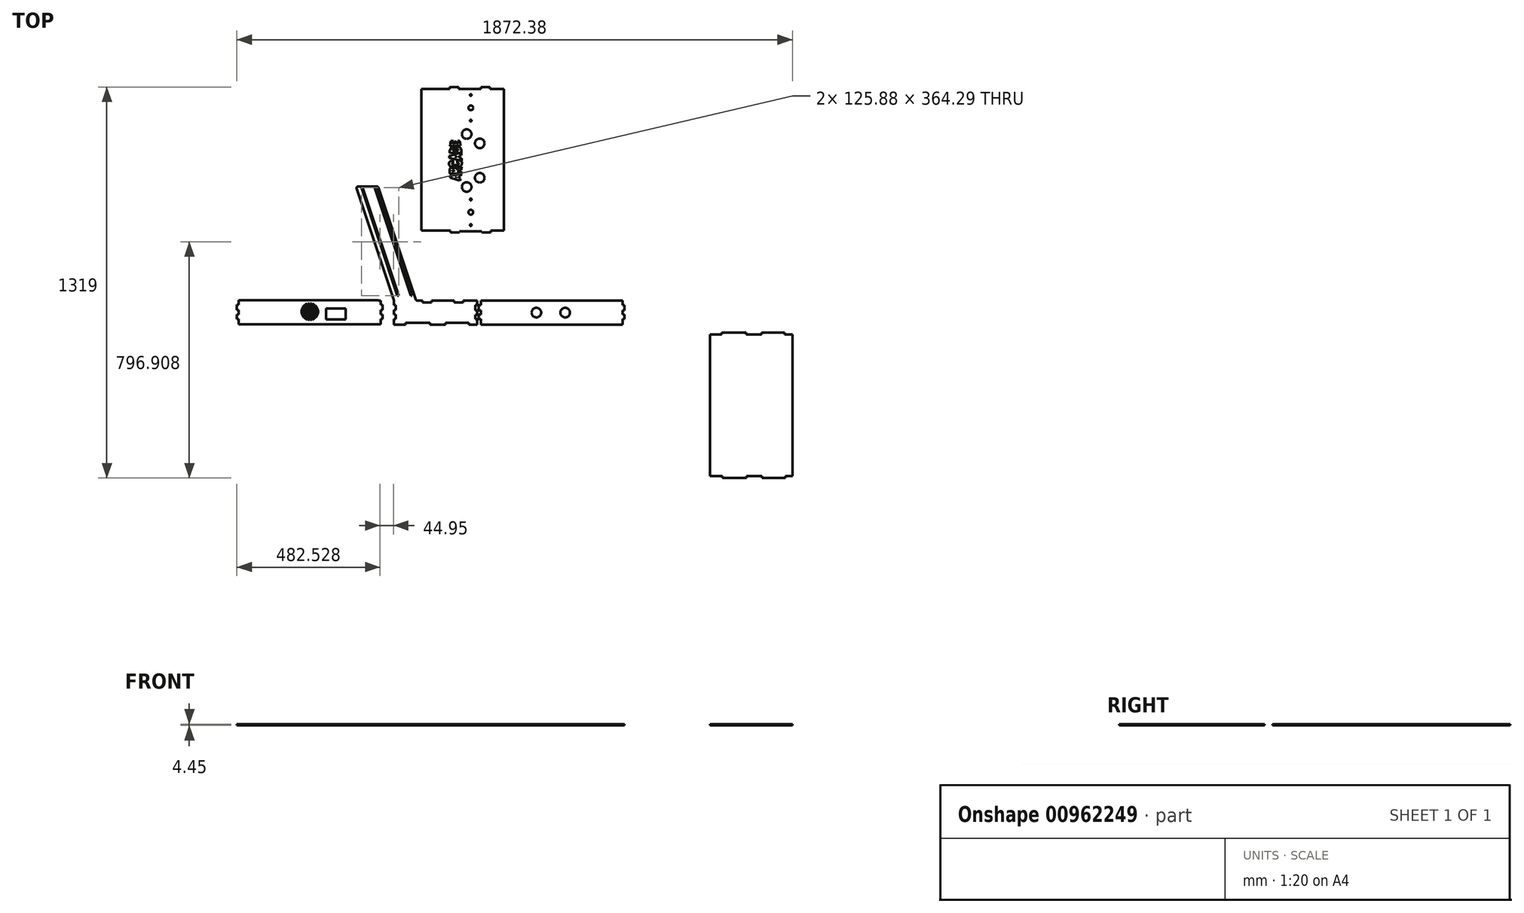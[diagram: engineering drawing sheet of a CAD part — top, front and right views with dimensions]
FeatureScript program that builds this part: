
annotation { "Feature Type Name" : "Feature", "Feature Type Description" : "" }
export const myFeature = defineFeature(function(context is Context, id is Id, definition is map)
    precondition{}
    {
        {
            var Q0;
            Q0=qCreatedBy(makeId("Top.planeOp"),FACE);
            var sketch = newSketch(context, id + "F0", { "sketchPlane" : qUnion([Q0])});
            skLineSegment(sketch, "E0.0", {"start": v(-133.22, 195.57) * mm, "end": v(-13.13, -164.7) * mm});
            skLineSegment(sketch, "E0.2", {"start": v(-206.4, 192.41) * mm, "end": v(-84, -174.81) * mm});
            skLineSegment(sketch, "E1", {"start": v(-84, -174.81) * mm, "end": v(-80.85, -184.23) * mm});
            skLineSegment(sketch, "E2", {"start": v(-13.13, -164.7) * mm, "end": v(-7.25, -182.33) * mm});
            skPoint(sketch, "E3.start.orphan", {"position": v(-23.94, -169.52) * mm});
            skLineSegment(sketch, "E4.bottom", {"start": v(-2.51, -185.75) * mm, "end": v(15.83, -185.75) * mm});
            skLineSegment(sketch, "E5", {"start": v(-129.53, 12.4) * mm, "end": v(-125.08, 12.4) * mm});
            skLineSegment(sketch, "E6", {"start": v(-89.03, 12.4) * mm, "end": v(-93.48, 12.4) * mm});
            skLineSegment(sketch, "E7.left", {"start": v(-80.35, -185.75) * mm, "end": v(-80.35, -201.04) * mm});
            skPoint(sketch, "E8.end.orphan", {"position": v(-48.56, -185.75) * mm});
            skLineSegment(sketch, "E9", {"start": v(-188.02, 199) * mm, "end": v(-201.66, 199) * mm});
            skLineSegment(sketch, "E10", {"start": v(-188.02, 199) * mm, "end": v(-137.97, 199) * mm});
            skPoint(sketch, "E11.start.orphan", {"position": v(-188.02, 194.54) * mm});
            skLineSegment(sketch, "E12.bottom", {"start": v(45.83, -192.08) * mm, "end": v(15.83, -192.08) * mm});
            skPoint(sketch, "E12.middle", {"position": v(31.62, -185.75) * mm});
            skPoint(sketch, "E13.middle", {"position": v(159.6, -185.75) * mm});
            skPoint(sketch, "E12.top.end.orphan", {"position": v(17.41, -179.42) * mm});
            skPoint(sketch, "E14.orphan", {"position": v(47.41, -179.42) * mm});
            skPoint(sketch, "E13.top.end.orphan", {"position": v(142.34, -174.18) * mm});
            skPoint(sketch, "E15.orphan", {"position": v(176.85, -174.18) * mm});
            skLineSegment(sketch, "E16.bottom", {"start": v(152.59, -192.08) * mm, "end": v(122.59, -192.08) * mm});
            skLineSegment(sketch, "E16.left", {"start": v(152.59, -192.08) * mm, "end": v(152.58, -185.75) * mm});
            skLineSegment(sketch, "E16.right", {"start": v(122.59, -192.08) * mm, "end": v(122.58, -185.75) * mm});
            skLineSegment(sketch, "E17.trimOffspring", {"start": v(47.28, -185.75) * mm, "end": v(122.58, -185.75) * mm});
            skLineSegment(sketch, "E18.trimOffspring", {"start": v(152.58, -185.75) * mm, "end": v(199.85, -185.75) * mm});
            skPoint(sketch, "E19.middle", {"position": v(199.48, -209.33) * mm});
            skPoint(sketch, "E19.left.end.orphan", {"position": v(205.95, -200.47) * mm});
            skPoint(sketch, "E20.orphan", {"position": v(205.67, -218.2) * mm});
            skLineSegment(sketch, "E21.bottom", {"start": v(109.66, 43.6) * mm, "end": v(139.96, 43.6) * mm});
            skLineSegment(sketch, "E21.left", {"start": v(109.66, 43.6) * mm, "end": v(109.66, 49.94) * mm});
            skLineSegment(sketch, "E21.right", {"start": v(139.96, 43.6) * mm, "end": v(139.96, 48.06) * mm});
            skLineSegment(sketch, "E22.top", {"start": v(214.96, 43.6) * mm, "end": v(245.26, 43.6) * mm});
            skLineSegment(sketch, "E22.left", {"start": v(214.96, 48.06) * mm, "end": v(214.96, 43.6) * mm});
            skLineSegment(sketch, "E22.right", {"start": v(245.26, 49.94) * mm, "end": v(245.26, 43.6) * mm});
            skLineSegment(sketch, "E23", {"start": v(86.13, 49.94) * mm, "end": v(109.66, 49.94) * mm});
            skLineSegment(sketch, "E24", {"start": v(139.96, 48.06) * mm, "end": v(214.96, 48.06) * mm});
            skLineSegment(sketch, "E25", {"start": v(245.26, 49.94) * mm, "end": v(289.7, 49.94) * mm});
            skLineSegment(sketch, "E26", {"start": v(289.7, 49.94) * mm, "end": v(289.7, 528.39) * mm});
            skLineSegment(sketch, "E27", {"start": v(86.13, 528.39) * mm, "end": v(107.63, 528.39) * mm});
            skLineSegment(sketch, "E28.MirrorCS", {"start": v(107.63, 534.72) * mm, "end": v(107.63, 528.39) * mm});
            skLineSegment(sketch, "E29.MirrorCS", {"start": v(137.93, 534.72) * mm, "end": v(137.93, 528.39) * mm});
            skLineSegment(sketch, "E30.MirrorCS", {"start": v(212.93, 528.39) * mm, "end": v(212.93, 534.72) * mm});
            skLineSegment(sketch, "E31.MirrorCS", {"start": v(243.23, 528.39) * mm, "end": v(243.23, 534.72) * mm});
            skLineSegment(sketch, "E32.trimOffspring", {"start": v(137.93, 528.39) * mm, "end": v(212.93, 528.39) * mm});
            skLineSegment(sketch, "E33.trimOffspring", {"start": v(243.23, 528.39) * mm, "end": v(289.7, 528.39) * mm});
            skPoint(sketch, "E34.start.orphan", {"position": v(86.13, 289.16) * mm});
            skCircle(sketch, "E35", {"center": v(178.38, 507.69) * mm, "radius": 3 * mm});
            skCircle(sketch, "E36", {"center": v(178.38, 421.29) * mm, "radius": 3 * mm});
            skCircle(sketch, "E37", {"center": v(164.4, 375.88) * mm, "radius": 16.13 * mm});
            skCircle(sketch, "E38", {"center": v(208.47, 344.63) * mm, "radius": 16.13 * mm});
            skCircle(sketch, "E39.MirrorC", {"center": v(178.38, 155.57) * mm, "radius": 3 * mm});
            skCircle(sketch, "E40.MirrorC", {"center": v(178.38, 69.17) * mm, "radius": 3 * mm});
            skCircle(sketch, "E41.MirrorC", {"center": v(208.47, 228.58) * mm, "radius": 16.13 * mm});
            skCircle(sketch, "E42.MirrorC", {"center": v(164.4, 197.33) * mm, "radius": 16.13 * mm});
            skCircle(sketch, "E43", {"center": v(178.38, 464.49) * mm, "radius": 8.09 * mm});
            skCircle(sketch, "E44.MirrorC", {"center": v(178.38, 112.37) * mm, "radius": 8.09 * mm});
            skLineSegment(sketch, "E45.MirrorCS", {"start": v(120.12, 254.5) * mm, "end": v(118.38, 254.37) * mm});
            skLineSegment(sketch, "E46.MirrorCS", {"start": v(146.92, 313.16) * mm, "end": v(146.92, 304.04) * mm});
            skLineSegment(sketch, "E47.MirrorCS", {"start": v(146.24, 313.22) * mm, "end": v(146.92, 313.16) * mm});
            skLineSegment(sketch, "E48.MirrorCS", {"start": v(117.25, 254.08) * mm, "end": v(116.34, 253.4) * mm});
            skLineSegment(sketch, "E49.MirrorCS", {"start": v(116.34, 253.4) * mm, "end": v(116, 250.63) * mm});
            skLineSegment(sketch, "E50.MirrorCS", {"start": v(129.87, 228.95) * mm, "end": v(129.87, 231.1) * mm});
            skLineSegment(sketch, "E51.MirrorCS", {"start": v(118.38, 254.37) * mm, "end": v(117.25, 254.08) * mm});
            skLineSegment(sketch, "E52.MirrorCS", {"start": v(121.7, 253.4) * mm, "end": v(120.12, 254.5) * mm});
            skLineSegment(sketch, "E53.MirrorCS", {"start": v(142.11, 234.25) * mm, "end": v(144.38, 234.25) * mm});
            skLineSegment(sketch, "E54.MirrorCS", {"start": v(123.2, 262.9) * mm, "end": v(122.67, 262.98) * mm});
            skLineSegment(sketch, "E55.MirrorCS", {"start": v(116, 250.63) * mm, "end": v(121.7, 250.43) * mm});
            skLineSegment(sketch, "E56.MirrorCS", {"start": v(144.64, 304.04) * mm, "end": v(140.36, 303.04) * mm});
            skLineSegment(sketch, "E57.MirrorCS", {"start": v(121.7, 250.43) * mm, "end": v(121.7, 253.4) * mm});
            skLineSegment(sketch, "E58.MirrorCS", {"start": v(130.78, 258.7) * mm, "end": v(128.56, 260.6) * mm});
            skLineSegment(sketch, "E59.MirrorCS", {"start": v(145.83, 241.97) * mm, "end": v(144.38, 234.25) * mm});
            skLineSegment(sketch, "E60.MirrorCS", {"start": v(138.33, 233.06) * mm, "end": v(142.11, 234.25) * mm});
            skLineSegment(sketch, "E61.MirrorCS", {"start": v(145.08, 255.03) * mm, "end": v(146.64, 255.34) * mm});
            skLineSegment(sketch, "E62.MirrorCS", {"start": v(142.65, 241.97) * mm, "end": v(145.83, 241.97) * mm});
            skLineSegment(sketch, "E63.MirrorCS", {"start": v(140.36, 296.24) * mm, "end": v(145.28, 294.98) * mm});
            skLineSegment(sketch, "E64.MirrorCS", {"start": v(146.92, 304.04) * mm, "end": v(144.64, 304.04) * mm});
            skLineSegment(sketch, "E65.MirrorCS", {"start": v(145.9, 250.5) * mm, "end": v(132.72, 250.5) * mm});
            skLineSegment(sketch, "E66.MirrorCS", {"start": v(140.36, 303.04) * mm, "end": v(140.36, 296.24) * mm});
            skLineSegment(sketch, "E67.MirrorCS", {"start": v(125.05, 299.5) * mm, "end": v(130.81, 298.2) * mm});
            skLineSegment(sketch, "E68.MirrorCS", {"start": v(129.87, 231.1) * mm, "end": v(125.64, 230.28) * mm});
            skLineSegment(sketch, "E69.MirrorCS", {"start": v(123, 224.26) * mm, "end": v(134.99, 220.38) * mm});
            skLineSegment(sketch, "E70.MirrorCS", {"start": v(145.28, 294.98) * mm, "end": v(147.53, 294.98) * mm});
            skLineSegment(sketch, "E71.MirrorCS", {"start": v(130.81, 298.2) * mm, "end": v(130.81, 300.81) * mm});
            skLineSegment(sketch, "E72.MirrorCS", {"start": v(145.62, 242.56) * mm, "end": v(145.9, 250.5) * mm});
            skLineSegment(sketch, "E73.MirrorCS", {"start": v(125.64, 230.28) * mm, "end": v(129.87, 228.95) * mm});
            skLineSegment(sketch, "E74.MirrorCS", {"start": v(141.03, 226.32) * mm, "end": v(137.8, 226.9) * mm});
            skLineSegment(sketch, "E75.MirrorCS", {"start": v(137.8, 226.9) * mm, "end": v(138.33, 233.06) * mm});
            skLineSegment(sketch, "E76.MirrorCS", {"start": v(132.72, 250.5) * mm, "end": v(145.08, 255.03) * mm});
            skLineSegment(sketch, "E77.MirrorCS", {"start": v(147.3, 264.53) * mm, "end": v(130.78, 258.7) * mm});
            skLineSegment(sketch, "E78.MirrorCS", {"start": v(146.64, 255.34) * mm, "end": v(147.3, 264.53) * mm});
            skLineSegment(sketch, "E79.MirrorCS", {"start": v(130.81, 300.81) * mm, "end": v(125.05, 299.5) * mm});
            skLineSegment(sketch, "E80.MirrorCS", {"start": v(143.46, 226.32) * mm, "end": v(141.03, 226.32) * mm});
            skLineSegment(sketch, "E81.MirrorCS", {"start": v(142.65, 241.97) * mm, "end": v(128.56, 238.4) * mm});
            skLineSegment(sketch, "E82.MirrorCS", {"start": v(140.12, 218.92) * mm, "end": v(141.84, 218.2) * mm});
            skLineSegment(sketch, "E83.MirrorCS", {"start": v(135.95, 321.28) * mm, "end": v(135.67, 323.92) * mm});
            skArc(sketch, "E84.MirrorCS", {"start": v(135.67, 323.92) * mm, "mid": v(126.36, 327.54) * mm, "end": v(117.25, 323.41) * mm});
            skLineSegment(sketch, "E85.MirrorCS", {"start": v(107.46, 243.91) * mm, "end": v(145.62, 242.56) * mm});
            skLineSegment(sketch, "E86.MirrorCS", {"start": v(141.84, 218.2) * mm, "end": v(143.46, 226.32) * mm});
            skFitSpline(sketch, "E87.MirrorCS", {"points": [v(128.56, 260.6) * mm, v(123.2, 262.9) * mm, v(114.65, 262.9) * mm, v(107.11, 257.92) * mm, v(107.34, 246.66) * mm, v(107.46, 243.91) * mm, v(131.36, 256.58) * mm, v(128.56, 260.6) * mm]});
            skLineSegment(sketch, "E88.MirrorCS", {"start": v(117.25, 321.28) * mm, "end": v(135.95, 321.28) * mm});
            skLineSegment(sketch, "E89.MirrorCS", {"start": v(131.27, 342.19) * mm, "end": v(130.03, 350.78) * mm});
            skArc(sketch, "E90.MirrorCS", {"start": v(146.24, 324.8) * mm, "mid": v(125.43, 335.33) * mm, "end": v(107.15, 320.84) * mm});
            skLineSegment(sketch, "E91.MirrorCS", {"start": v(108.97, 235.06) * mm, "end": v(109.67, 228.58) * mm});
            skLineSegment(sketch, "E92.MirrorCS", {"start": v(117.25, 341.92) * mm, "end": v(119.47, 353.18) * mm});
            skLineSegment(sketch, "E93.MirrorCS", {"start": v(122.84, 350.78) * mm, "end": v(122.84, 341.92) * mm});
            skLineSegment(sketch, "E94.MirrorCS", {"start": v(134.15, 353.36) * mm, "end": v(135.67, 342.82) * mm});
            skLineSegment(sketch, "E95.MirrorCS", {"start": v(109.67, 228.58) * mm, "end": v(123, 224.26) * mm});
            skLineSegment(sketch, "E96.MirrorCS", {"start": v(119.47, 353.18) * mm, "end": v(111.45, 352.62) * mm});
            skLineSegment(sketch, "E97.MirrorCS", {"start": v(135.67, 342.82) * mm, "end": v(131.27, 342.19) * mm});
            skLineSegment(sketch, "E98.MirrorCS", {"start": v(117.25, 323.41) * mm, "end": v(117.25, 321.28) * mm});
            skLineSegment(sketch, "E99.MirrorCS", {"start": v(147.5, 285.67) * mm, "end": v(105.6, 295.49) * mm});
            skLineSegment(sketch, "E100.MirrorCS", {"start": v(141.7, 353.36) * mm, "end": v(134.15, 353.36) * mm});
            skLineSegment(sketch, "E101.MirrorCS", {"start": v(105.6, 295.49) * mm, "end": v(105.6, 302.4) * mm});
            skLineSegment(sketch, "E102.MirrorCS", {"start": v(130.03, 350.78) * mm, "end": v(122.84, 350.78) * mm});
            skLineSegment(sketch, "E103.MirrorCS", {"start": v(128.56, 238.4) * mm, "end": v(108.97, 235.06) * mm});
            skLineSegment(sketch, "E104.MirrorCS", {"start": v(122.84, 341.92) * mm, "end": v(117.25, 341.92) * mm});
            skLineSegment(sketch, "E105.MirrorCS", {"start": v(111.45, 352.62) * mm, "end": v(108.28, 334.85) * mm});
            skLineSegment(sketch, "E106.MirrorCS", {"start": v(134.99, 220.38) * mm, "end": v(140.12, 218.92) * mm});
            skLineSegment(sketch, "E107.MirrorCS", {"start": v(146.92, 313.7) * mm, "end": v(146.24, 324.8) * mm});
            skLineSegment(sketch, "E108.MirrorCS", {"start": v(105.6, 302.4) * mm, "end": v(146.24, 313.22) * mm});
            skLineSegment(sketch, "E109.MirrorCS", {"start": v(106.5, 312.6) * mm, "end": v(146.92, 313.7) * mm});
            skLineSegment(sketch, "E110.MirrorCS", {"start": v(106.5, 312.6) * mm, "end": v(107.15, 320.84) * mm});
            skLineSegment(sketch, "E111.MirrorCS", {"start": v(143.98, 337.2) * mm, "end": v(141.7, 353.36) * mm});
            skLineSegment(sketch, "E112.MirrorCS", {"start": v(108.28, 334.85) * mm, "end": v(143.98, 337.2) * mm});
            skFitSpline(sketch, "E113.MirrorC", {"points": [v(118.4, 278.2) * mm, v(116.6, 278.05) * mm, v(114.9, 277.2) * mm, v(114.56, 275.62) * mm, v(115.92, 274) * mm, v(121.92, 272.13) * mm, v(128.49, 271.77) * mm, v(134.71, 272.58) * mm, v(138, 274.5) * mm, v(138.34, 276.84) * mm, v(135.73, 277.9) * mm, v(132.68, 278.86) * mm, v(132.68, 279.68) * mm, v(132.62, 286.61) * mm, v(132.68, 287.83) * mm, v(142.87, 285.6) * mm, v(143.54, 285.19) * mm, v(147.96, 281.4) * mm, v(148.3, 273.3) * mm, v(145.36, 268.33) * mm, v(137.77, 264.48) * mm, v(126.67, 263.32) * mm, v(115.01, 264.89) * mm, v(108.45, 268.48) * mm, v(105.05, 272.38) * mm, v(104.54, 276.89) * mm, v(106.18, 281.85) * mm, v(112.01, 286) * mm, v(117.28, 287.53) * mm, v(118.4, 287.58) * mm, v(118.64, 285.19) * mm, v(118.4, 278.2) * mm]});
            skLineSegment(sketch, "E114", {"start": v(147.53, 294.98) * mm, "end": v(147.5, 285.67) * mm});
            skLineSegment(sketch, "E115.bottom", {"start": v(211.85, -185.75) * mm, "end": v(690.3, -185.75) * mm});
            skLineSegment(sketch, "E115.top", {"start": v(211.85, -266.77) * mm, "end": v(690.3, -266.77) * mm});
            skLineSegment(sketch, "E115.left", {"start": v(211.85, -185.75) * mm, "end": v(211.85, -200.65) * mm});
            skLineSegment(sketch, "E115.right", {"start": v(690.3, -185.75) * mm, "end": v(690.3, -200.9) * mm});
            skLineSegment(sketch, "E116.top", {"start": v(211.85, -218.2) * mm, "end": v(205.52, -218.2) * mm});
            skLineSegment(sketch, "E117.top", {"start": v(211.85, -248.5) * mm, "end": v(205.52, -248.5) * mm});
            skLineSegment(sketch, "E117.right", {"start": v(205.52, -233.2) * mm, "end": v(205.52, -248.5) * mm});
            skCircle(sketch, "E118", {"center": v(399.44, -226.26) * mm, "radius": 16.13 * mm});
            skPoint(sketch, "E118.centerSnap0", {"position": v(211.85, -226.26) * mm});
            skCircle(sketch, "E119.MirrorC", {"center": v(496.38, -226.26) * mm, "radius": 16.13 * mm});
            skPoint(sketch, "E120.start.orphan", {"position": v(451.07, -185.75) * mm});
            skLineSegment(sketch, "E121.MirrorCS", {"start": v(690.3, -233.2) * mm, "end": v(696.63, -233.2) * mm});
            skLineSegment(sketch, "E122.MirrorCS", {"start": v(690.3, -248.5) * mm, "end": v(696.63, -248.5) * mm});
            skLineSegment(sketch, "E123.MirrorCS", {"start": v(690.3, -218.2) * mm, "end": v(696.63, -218.2) * mm});
            skLineSegment(sketch, "E124.MirrorCS", {"start": v(690.3, -200.9) * mm, "end": v(696.63, -200.9) * mm});
            skLineSegment(sketch, "E125.trimOffspring", {"start": v(211.85, -218.2) * mm, "end": v(211.85, -226.26) * mm});
            skLineSegment(sketch, "E126.trimOffspring", {"start": v(211.85, -248.5) * mm, "end": v(211.85, -266.77) * mm});
            skLineSegment(sketch, "E127.trimOffspring", {"start": v(690.3, -248.5) * mm, "end": v(690.3, -266.77) * mm});
            skLineSegment(sketch, "E128.trimOffspring", {"start": v(690.3, -218.2) * mm, "end": v(690.3, -233.2) * mm});
            skPoint(sketch, "E129.start.orphan", {"position": v(58.75, -264.57) * mm});
            skPoint(sketch, "E130.middle", {"position": v(-577.81, -208.7) * mm});
            skPoint(sketch, "E130.left.end.orphan", {"position": v(-573.36, -199.94) * mm});
            skPoint(sketch, "E131.orphan", {"position": v(-573.36, -217.46) * mm});
            skLineSegment(sketch, "E132.bottom", {"start": v(-603.58, -184.65) * mm, "end": v(-133.22, -184.65) * mm});
            skLineSegment(sketch, "E132.top", {"start": v(-603.58, -265.67) * mm, "end": v(-125.08, -265.67) * mm});
            skLineSegment(sketch, "E132.left", {"start": v(-603.58, -184.65) * mm, "end": v(-603.58, -199.79) * mm});
            skLineSegment(sketch, "E132.right", {"start": v(-125.08, -185.75) * mm, "end": v(-125.08, -199.79) * mm});
            skLineSegment(sketch, "E133.bottom", {"start": v(-603.58, -199.79) * mm, "end": v(-609.9, -199.79) * mm});
            skLineSegment(sketch, "E133.top", {"start": v(-603.58, -217.09) * mm, "end": v(-609.9, -217.09) * mm});
            skLineSegment(sketch, "E133.right", {"start": v(-609.9, -199.79) * mm, "end": v(-609.9, -217.09) * mm});
            skLineSegment(sketch, "E134.bottom", {"start": v(-603.58, -232.09) * mm, "end": v(-609.9, -232.09) * mm});
            skLineSegment(sketch, "E134.top", {"start": v(-603.58, -247.39) * mm, "end": v(-609.9, -247.39) * mm});
            skLineSegment(sketch, "E134.right", {"start": v(-609.9, -232.09) * mm, "end": v(-609.9, -247.39) * mm});
            skPoint(sketch, "E135.centerSnap0", {"position": v(-563.42, -225.16) * mm});
            skPoint(sketch, "E136.start.orphan", {"position": v(-324.17, -184.65) * mm});
            skLineSegment(sketch, "E137.MirrorCS", {"start": v(-125.08, -247.39) * mm, "end": v(-118.75, -247.39) * mm});
            skLineSegment(sketch, "E138.MirrorCS", {"start": v(-125.08, -217.09) * mm, "end": v(-118.75, -217.09) * mm});
            skLineSegment(sketch, "E139.MirrorCS", {"start": v(-125.08, -199.79) * mm, "end": v(-118.75, -199.79) * mm});
            skLineSegment(sketch, "E140.trimOffspring", {"start": v(-603.58, -217.09) * mm, "end": v(-603.58, -232.09) * mm});
            skLineSegment(sketch, "E141.trimOffspring", {"start": v(-603.58, -247.39) * mm, "end": v(-603.58, -265.67) * mm});
            skLineSegment(sketch, "E142.trimOffspring", {"start": v(-125.08, -247.39) * mm, "end": v(-125.08, -265.67) * mm});
            skLineSegment(sketch, "E143.trimOffspring", {"start": v(-125.08, -217.09) * mm, "end": v(-125.08, -229.04) * mm});
            skPoint(sketch, "E144.middle", {"position": v(0, -266.77) * mm});
            skPoint(sketch, "E145.orphan", {"position": v(1023.86, -273.1) * mm});
            skPoint(sketch, "E146.orphan", {"position": v(1106.14, -273.1) * mm});
            skLineSegment(sketch, "E147.bottom", {"start": v(984.65, -299.5) * mm, "end": v(1023.86, -299.5) * mm});
            skLineSegment(sketch, "E147.left", {"start": v(984.65, -299.5) * mm, "end": v(984.65, -773.5) * mm});
            skLineSegment(sketch, "E148.top", {"start": v(1158.16, -293.17) * mm, "end": v(1236.46, -293.17) * mm});
            skLineSegment(sketch, "E148.left", {"start": v(1158.16, -299.5) * mm, "end": v(1158.16, -293.17) * mm});
            skLineSegment(sketch, "E149.trimOffspring", {"start": v(1106.16, -299.5) * mm, "end": v(1158.16, -299.5) * mm});
            skLineSegment(sketch, "E150.trimOffspring", {"start": v(1240.66, -299.5) * mm, "end": v(1262.47, -299.5) * mm});
            skLineSegment(sketch, "E151.MirrorCS", {"start": v(1026.07, -773.5) * mm, "end": v(1026.07, -777.95) * mm});
            skLineSegment(sketch, "E152.MirrorCS", {"start": v(1108.37, -777.95) * mm, "end": v(1108.37, -784.28) * mm});
            skLineSegment(sketch, "E153.MirrorCS", {"start": v(1160.37, -777.95) * mm, "end": v(1160.37, -784.28) * mm});
            skLineSegment(sketch, "E154.MirrorCS", {"start": v(1238.67, -777.95) * mm, "end": v(1238.67, -784.28) * mm});
            skLineSegment(sketch, "E155.trimOffspring", {"start": v(1108.37, -777.95) * mm, "end": v(1160.37, -777.95) * mm});
            skPoint(sketch, "E156.start.orphan", {"position": v(984.65, -536.5) * mm});
            skLineSegment(sketch, "E157.trimOffspring", {"start": v(1238.67, -777.95) * mm, "end": v(1262.47, -777.95) * mm});
            skLineSegment(sketch, "E158", {"start": v(696.63, -200.9) * mm, "end": v(696.63, -218.2) * mm});
            skLineSegment(sketch, "E159", {"start": v(696.63, -233.2) * mm, "end": v(696.63, -248.5) * mm});
            skLineSegment(sketch, "E160", {"start": v(-118.75, -217.09) * mm, "end": v(-118.75, -199.79) * mm});
            skLineSegment(sketch, "E161", {"start": v(-118.75, -232.09) * mm, "end": v(-118.75, -247.39) * mm});
            skLineSegment(sketch, "E162", {"start": v(107.63, 534.72) * mm, "end": v(137.93, 534.72) * mm});
            skLineSegment(sketch, "E163", {"start": v(212.93, 534.72) * mm, "end": v(243.23, 534.72) * mm});
            skLineSegment(sketch, "E164", {"start": v(1238.67, -784.28) * mm, "end": v(1160.37, -784.28) * mm});
            skLineSegment(sketch, "E165", {"start": v(1108.37, -784.28) * mm, "end": v(1026.07, -784.28) * mm});
            skLineSegment(sketch, "E166", {"start": v(1026.07, -784.28) * mm, "end": v(1026.07, -777.95) * mm});
            skLineSegment(sketch, "E167", {"start": v(984.65, -773.5) * mm, "end": v(984.65, -777.95) * mm});
            skLineSegment(sketch, "E168", {"start": v(984.65, -777.95) * mm, "end": v(1026.07, -777.95) * mm});
            skLineSegment(sketch, "E169.bottom", {"start": v(86.13, 49.94) * mm, "end": v(11.9, 49.94) * mm});
            skLineSegment(sketch, "E169.top", {"start": v(86.13, 528.39) * mm, "end": v(11.9, 528.39) * mm});
            skLineSegment(sketch, "E169.right", {"start": v(11.9, 49.94) * mm, "end": v(11.9, 528.39) * mm});
            skLineSegment(sketch, "E170", {"start": v(-190.32, 194.78) * mm, "end": v(-68.9, -169.52) * mm});
            skLineSegment(sketch, "E171", {"start": v(-64.44, -169.52) * mm, "end": v(-68.9, -169.52) * mm});
            skLineSegment(sketch, "E172", {"start": v(-125.16, 12.63) * mm, "end": v(-185.87, 194.78) * mm});
            skLineSegment(sketch, "E173", {"start": v(-125.16, 12.63) * mm, "end": v(-64.44, -169.52) * mm});
            skLineSegment(sketch, "E174.trimOffspring", {"start": v(-185.87, 194.78) * mm, "end": v(-190.32, 194.78) * mm});
            skLineSegment(sketch, "E175", {"start": v(-140.92, 194.78) * mm, "end": v(-19.5, -169.52) * mm});
            skLineSegment(sketch, "E176", {"start": v(-140.92, 194.78) * mm, "end": v(-145.37, 194.78) * mm});
            skLineSegment(sketch, "E177", {"start": v(-23.94, -169.52) * mm, "end": v(-19.5, -169.52) * mm});
            skLineSegment(sketch, "E178", {"start": v(-84.66, 12.63) * mm, "end": v(-23.94, -169.52) * mm});
            skLineSegment(sketch, "E179", {"start": v(-84.66, 12.63) * mm, "end": v(-145.37, 194.78) * mm});
            skLineSegment(sketch, "E180.top", {"start": v(1023.86, -293.17) * mm, "end": v(1106.16, -293.17) * mm});
            skLineSegment(sketch, "E180.left", {"start": v(1023.86, -299.5) * mm, "end": v(1023.86, -293.17) * mm});
            skLineSegment(sketch, "E180.right", {"start": v(1106.16, -299.5) * mm, "end": v(1106.16, -293.17) * mm});
            skLineSegment(sketch, "E181.MirrorCS", {"start": v(1236.46, -293.17) * mm, "end": v(1158.16, -293.17) * mm});
            skPoint(sketch, "E182.start.orphan", {"position": v(1132.16, -299.5) * mm});
            skPoint(sketch, "E183.orphan", {"position": v(211.85, -232.77) * mm});
            skLineSegment(sketch, "E184", {"start": v(211.85, -218.2) * mm, "end": v(211.85, -230.2) * mm});
            skArc(sketch, "E185", {"start": v(-357.93, -195.94) * mm, "mid": v(-360.4, -195.47) * mm, "end": v(-362.9, -195.23) * mm});
            skPoint(sketch, "E185.centerSnap0", {"position": v(-125.08, -223.06) * mm});
            skPoint(sketch, "E185.centerSnap1", {"position": v(-364.33, -184.65) * mm});
            skLineSegment(sketch, "E186.left", {"start": v(-362.9, -250.9) * mm, "end": v(-362.9, -195.23) * mm});
            skLineSegment(sketch, "E186.right", {"start": v(-365.76, -250.9) * mm, "end": v(-365.76, -195.23) * mm});
            skLineSegment(sketch, "E187.left", {"start": v(-355.09, -249.36) * mm, "end": v(-355.09, -196.77) * mm});
            skLineSegment(sketch, "E187.right", {"start": v(-357.93, -250.19) * mm, "end": v(-357.93, -195.94) * mm});
            skPoint(sketch, "E187.middle", {"position": v(-356.5, -223.06) * mm});
            skPoint(sketch, "E187.middle.positionSnap0", {"position": v(-362.9, -223.06) * mm});
            skPoint(sketch, "E187.centerSnap0", {"position": v(-362.9, -223.06) * mm});
            skLineSegment(sketch, "E188.left", {"start": v(-348.17, -245.77) * mm, "end": v(-348.17, -200.36) * mm});
            skLineSegment(sketch, "E188.right", {"start": v(-345.33, -243.45) * mm, "end": v(-345.33, -202.68) * mm});
            skPoint(sketch, "E188.middle", {"position": v(-346.75, -223.06) * mm});
            skLineSegment(sketch, "E189.MirrorCS", {"start": v(-370.73, -250.19) * mm, "end": v(-370.73, -195.94) * mm});
            skLineSegment(sketch, "E190.MirrorCS", {"start": v(-373.57, -249.36) * mm, "end": v(-373.57, -196.77) * mm});
            skLineSegment(sketch, "E191.MirrorCS", {"start": v(-380.5, -245.77) * mm, "end": v(-380.5, -200.36) * mm});
            skLineSegment(sketch, "E192.MirrorCS", {"start": v(-383.33, -243.45) * mm, "end": v(-383.33, -202.68) * mm});
            skPoint(sketch, "E186.top.end.orphan", {"position": v(-365.76, -191.24) * mm});
            skPoint(sketch, "E186.top.start.orphan", {"position": v(-362.9, -191.24) * mm});
            skPoint(sketch, "E193.orphan", {"position": v(-370.73, -190.18) * mm});
            skPoint(sketch, "E194.orphan", {"position": v(-373.57, -190.18) * mm});
            skPoint(sketch, "E195.orphan", {"position": v(-383.33, -193.02) * mm});
            skPoint(sketch, "E196.orphan", {"position": v(-380.5, -193.02) * mm});
            skPoint(sketch, "E187.top.end.orphan", {"position": v(-357.93, -190.18) * mm});
            skPoint(sketch, "E187.top.start.orphan", {"position": v(-355.09, -190.18) * mm});
            skPoint(sketch, "E188.top.end.orphan", {"position": v(-345.33, -193.02) * mm});
            skPoint(sketch, "E188.top.start.orphan", {"position": v(-348.17, -193.02) * mm});
            skArc(sketch, "E197.trimOffspring", {"start": v(-365.76, -195.23) * mm, "mid": v(-368.26, -195.47) * mm, "end": v(-370.73, -195.94) * mm});
            skArc(sketch, "E198.trimOffspring", {"start": v(-383.33, -202.68) * mm, "mid": v(-392.2, -223.06) * mm, "end": v(-383.33, -243.45) * mm});
            skArc(sketch, "E199.trimOffspring", {"start": v(-370.73, -250.19) * mm, "mid": v(-368.26, -250.65) * mm, "end": v(-365.76, -250.9) * mm});
            skArc(sketch, "E200.trimOffspring", {"start": v(-362.9, -250.9) * mm, "mid": v(-360.4, -250.65) * mm, "end": v(-357.93, -250.19) * mm});
            skArc(sketch, "E201.trimOffspring", {"start": v(-355.09, -249.36) * mm, "mid": v(-351.5, -247.8) * mm, "end": v(-348.17, -245.77) * mm});
            skArc(sketch, "E202.trimOffspring", {"start": v(-345.33, -243.45) * mm, "mid": v(-337.05, -217.36) * mm, "end": v(-355.09, -196.77) * mm});
            skPoint(sketch, "E203.orphan", {"position": v(-370.73, -255.95) * mm});
            skPoint(sketch, "E204.orphan", {"position": v(-373.57, -255.95) * mm});
            skPoint(sketch, "E205.orphan", {"position": v(-380.5, -253.1) * mm});
            skPoint(sketch, "E206.orphan", {"position": v(-383.33, -253.1) * mm});
            skPoint(sketch, "E207.orphan", {"position": v(-362.9, -254.88) * mm});
            skPoint(sketch, "E208.orphan", {"position": v(-357.93, -255.95) * mm});
            skPoint(sketch, "E209.orphan", {"position": v(-355.09, -255.95) * mm});
            skPoint(sketch, "E188.bottom.start.orphan", {"position": v(-348.17, -253.1) * mm});
            skPoint(sketch, "E210.orphan", {"position": v(-345.33, -253.1) * mm});
            skPoint(sketch, "E211.orphan", {"position": v(-365.76, -254.88) * mm});
            skArc(sketch, "E212.trimOffspring", {"start": v(-380.5, -245.77) * mm, "mid": v(-377.16, -247.8) * mm, "end": v(-373.57, -249.36) * mm});
            skArc(sketch, "E213", {"start": v(-373.57, -196.77) * mm, "mid": v(-377.47, -197.73) * mm, "end": v(-380.5, -200.36) * mm});
            skLineSegment(sketch, "E214.bottom", {"start": v(-242.86, -248.61) * mm, "end": v(-309.57, -248.61) * mm});
            skLineSegment(sketch, "E214.top", {"start": v(-242.86, -212.3) * mm, "end": v(-309.57, -212.3) * mm});
            skLineSegment(sketch, "E214.left", {"start": v(-242.86, -248.61) * mm, "end": v(-242.86, -212.3) * mm});
            skLineSegment(sketch, "E214.right", {"start": v(-309.57, -248.61) * mm, "end": v(-309.57, -212.3) * mm});
            skPoint(sketch, "E214.middle", {"position": v(-276.22, -230.46) * mm});
            skPoint(sketch, "E215.visualSharp", {"position": v(-208.6, 199) * mm});
            skArc(sketch, "E215.filletArc", {"start": v(-201.66, 199) * mm, "mid": v(-205.71, 196.92) * mm, "end": v(-206.4, 192.41) * mm});
            skPoint(sketch, "E216.visualSharp", {"position": v(-134.36, 199) * mm});
            skArc(sketch, "E216.filletArc", {"start": v(-133.22, 195.57) * mm, "mid": v(-135.04, 198.05) * mm, "end": v(-137.97, 199) * mm});
            skPoint(sketch, "E217.visualSharp", {"position": v(-6.11, -185.75) * mm});
            skArc(sketch, "E217.filletArc", {"start": v(-7.25, -182.33) * mm, "mid": v(-5.43, -184.8) * mm, "end": v(-2.51, -185.75) * mm});
            skLineSegment(sketch, "E218", {"start": v(45.83, -192.08) * mm, "end": v(45.83, -185.75) * mm});
            skLineSegment(sketch, "E219", {"start": v(15.83, -192.08) * mm, "end": v(15.83, -185.75) * mm});
            skLineSegment(sketch, "E220", {"start": v(16.32, -185.75) * mm, "end": v(15.83, -185.75) * mm});
            skLineSegment(sketch, "E221", {"start": v(-118.75, -232.09) * mm, "end": v(-125.08, -232.09) * mm});
            skLineSegment(sketch, "E222", {"start": v(-125.08, -232.09) * mm, "end": v(-125.08, -229.04) * mm});
            skPoint(sketch, "E223.middle", {"position": v(-69.63, -221.14) * mm});
            skPoint(sketch, "E223.middle.positionSnap0", {"position": v(-79.2, -221.14) * mm});
            skPoint(sketch, "E223.centerSnap0", {"position": v(-79.2, -221.14) * mm});
            skPoint(sketch, "E224.orphan", {"position": v(-79.2, -227.34) * mm});
            skPoint(sketch, "E225.MirrorCS.end.orphan", {"position": v(-74.72, -215.04) * mm});
            skPoint(sketch, "E225.MirrorCS.start.orphan", {"position": v(-79.2, -214.94) * mm});
            skLineSegment(sketch, "E226", {"start": v(-75.9, -230.97) * mm, "end": v(-75.9, -230.86) * mm});
            skLineSegment(sketch, "E227", {"start": v(-75.9, -215.57) * mm, "end": v(-75.9, -215.66) * mm});
            skLineSegment(sketch, "E228", {"start": v(-76.34, -243.08) * mm, "end": v(-76.34, -244.08) * mm});
            skLineSegment(sketch, "E229", {"start": v(1240.66, -299.5) * mm, "end": v(1236.46, -299.5) * mm});
            skLineSegment(sketch, "E230", {"start": v(1236.46, -299.5) * mm, "end": v(1236.46, -293.17) * mm});
            skLineSegment(sketch, "E231", {"start": v(1262.47, -299.5) * mm, "end": v(1262.47, -777.95) * mm});
            skPoint(sketch, "E232.MirrorCS.start.orphan", {"position": v(172.76, -266.77) * mm});
            skPoint(sketch, "E233.orphan", {"position": v(93.97, -266.77) * mm});
            skPoint(sketch, "E144.top.start.orphan", {"position": v(41.14, -260.44) * mm});
            skPoint(sketch, "E144.right.end.orphan", {"position": v(-41.14, -260.44) * mm});
            skLineSegment(sketch, "E234.bottom", {"start": v(-80.35, -266.77) * mm, "end": v(-40.94, -266.77) * mm});
            skLineSegment(sketch, "E235.top", {"start": v(93.36, -260.44) * mm, "end": v(171.36, -260.44) * mm});
            skLineSegment(sketch, "E235.left", {"start": v(93.36, -266.77) * mm, "end": v(93.36, -260.44) * mm});
            skLineSegment(sketch, "E236.trimOffspring", {"start": v(41.06, -266.77) * mm, "end": v(93.36, -266.77) * mm});
            skLineSegment(sketch, "E237.top", {"start": v(-40.94, -260.44) * mm, "end": v(41.06, -260.44) * mm});
            skLineSegment(sketch, "E237.left", {"start": v(-40.94, -266.77) * mm, "end": v(-40.94, -260.44) * mm});
            skLineSegment(sketch, "E237.right", {"start": v(41.06, -266.77) * mm, "end": v(41.06, -260.44) * mm});
            skLineSegment(sketch, "E238", {"start": v(171.36, -266.37) * mm, "end": v(171.36, -260.44) * mm});
            skLineSegment(sketch, "E239.left", {"start": v(-80.35, -185.14) * mm, "end": v(-80.35, -200.43) * mm});
            skLineSegment(sketch, "E240.MirrorCS", {"start": v(-74.02, -247.73) * mm, "end": v(-74.02, -232.73) * mm});
            skLineSegment(sketch, "E241.MirrorCS", {"start": v(-80.35, -200.43) * mm, "end": v(-74.02, -200.43) * mm});
            skLineSegment(sketch, "E242.trimOffspring", {"start": v(-80.35, -248.73) * mm, "end": v(-80.35, -267.01) * mm});
            skLineSegment(sketch, "E243", {"start": v(-80.35, -232.73) * mm, "end": v(-74.02, -232.73) * mm});
            skLineSegment(sketch, "E244", {"start": v(-74.02, -217.43) * mm, "end": v(-80.35, -217.43) * mm});
            skLineSegment(sketch, "E245", {"start": v(-80.35, -217.43) * mm, "end": v(-80.35, -232.73) * mm});
            skLineSegment(sketch, "E246", {"start": v(-74.02, -247.73) * mm, "end": v(-80.35, -247.73) * mm});
            skLineSegment(sketch, "E247", {"start": v(-80.35, -247.73) * mm, "end": v(-80.35, -248.73) * mm});
            skLineSegment(sketch, "E248", {"start": v(-74.02, -217.43) * mm, "end": v(-74.02, -200.43) * mm});
            skLineSegment(sketch, "E249", {"start": v(-80.35, -185.75) * mm, "end": v(-80.35, -184.23) * mm});
            skLineSegment(sketch, "E250", {"start": v(-80.35, -184.23) * mm, "end": v(-80.85, -184.23) * mm});
            skLineSegment(sketch, "E251", {"start": v(211.85, -230.2) * mm, "end": v(211.85, -232.77) * mm});
            skPoint(sketch, "E252.top.start.orphan", {"position": v(199.1, -232.77) * mm});
            skPoint(sketch, "E253.end.orphan", {"position": v(199.62, -233.2) * mm});
            skLineSegment(sketch, "E254", {"start": v(199.1, -232.77) * mm, "end": v(199.34, -232.77) * mm});
            skPoint(sketch, "E255.trimOffspring.end.orphan", {"position": v(198.57, -266.77) * mm});
            skPoint(sketch, "E252.bottom.end.orphan", {"position": v(193, -248.32) * mm});
            skPoint(sketch, "E252.bottom.start.orphan", {"position": v(198.86, -248.5) * mm});
            skLineSegment(sketch, "E256", {"start": v(171.36, -266.37) * mm, "end": v(199.48, -266.37) * mm});
            skLineSegment(sketch, "E257", {"start": v(199.48, -266.37) * mm, "end": v(199.48, -248.5) * mm});
            skLineSegment(sketch, "E258", {"start": v(199.48, -248.5) * mm, "end": v(193.15, -248.5) * mm});
            skLineSegment(sketch, "E259", {"start": v(193.15, -248.5) * mm, "end": v(193.15, -233.5) * mm});
            skPoint(sketch, "E19.right.start.orphan", {"position": v(193, -218.2) * mm});
            skPoint(sketch, "E260.start.orphan", {"position": v(193.29, -218.2) * mm});
            skPoint(sketch, "E19.top.end.orphan", {"position": v(193.29, -200.47) * mm});
            skPoint(sketch, "E19.top.start.orphan", {"position": v(199.62, -200.65) * mm});
            skLineSegment(sketch, "E261", {"start": v(199.85, -185.75) * mm, "end": v(199.85, -200.65) * mm});
            skLineSegment(sketch, "E262", {"start": v(193.15, -201.2) * mm, "end": v(193.15, -218.2) * mm});
            skLineSegment(sketch, "E263", {"start": v(205.52, -218.2) * mm, "end": v(205.52, -200.9) * mm});
            skLineSegment(sketch, "E264", {"start": v(205.52, -200.9) * mm, "end": v(211.85, -200.9) * mm});
            skLineSegment(sketch, "E265", {"start": v(211.85, -200.9) * mm, "end": v(211.85, -200.65) * mm});
            skPoint(sketch, "E116.bottom.end.orphan", {"position": v(205.52, -200.65) * mm});
            skLineSegment(sketch, "E266", {"start": v(205.52, -233.2) * mm, "end": v(211.85, -233.2) * mm});
            skLineSegment(sketch, "E267", {"start": v(211.85, -233.2) * mm, "end": v(211.85, -232.77) * mm});
            skLineSegment(sketch, "E268", {"start": v(193.15, -218.2) * mm, "end": v(199.48, -218.2) * mm});
            skLineSegment(sketch, "E269", {"start": v(199.48, -218.2) * mm, "end": v(199.48, -233.5) * mm});
            skLineSegment(sketch, "E270", {"start": v(199.48, -233.5) * mm, "end": v(193.15, -233.5) * mm});
            skLineSegment(sketch, "E271", {"start": v(45.83, -185.75) * mm, "end": v(47.28, -185.75) * mm});
            skLineSegment(sketch, "E272", {"start": v(193.15, -201.2) * mm, "end": v(199.85, -201.2) * mm});
            skLineSegment(sketch, "E273", {"start": v(199.85, -201.2) * mm, "end": v(199.85, -200.65) * mm});
            skLineSegment(sketch, "E274", {"start": v(-125.08, -185.75) * mm, "end": v(-133.22, -185.75) * mm});
            skLineSegment(sketch, "E275", {"start": v(-133.22, -185.75) * mm, "end": v(-133.22, -184.65) * mm});
            skPoint(sketch, "E276.orphan", {"position": v(-125.08, -184.65) * mm});
            skSolve(sketch);
        }
        {
            var Q0;
            Q0=makeQuery(id+"F0.imprint","IMPRINT",FACE,{"disambiguationData":[TD([[makeQuery(id+"F0.imprint","IMPRINT",EDGE,{"derivedFrom":sQuery(id+"F0.wireOp",EDGE,"E147.bottom")}),-1.0]])]});
            var Q1;
            Q1=makeQuery(id+"F0.imprint","IMPRINT",FACE,{"disambiguationData":[TD([[makeQuery(id+"F0.imprint","IMPRINT",EDGE,{"derivedFrom":sQuery(id+"F0.wireOp",EDGE,"E132.bottom")}),-1.0]])]});
            var Q2;
            {var subQ4=sQuery(id+"F0.wireOp",EDGE,"sC4kQ6F8-xUsw-eNn1-kUFQ-Rawnznmu5okk");Q2=makeQuery(id+"F0.imprint","IMPRINT",FACE,{"disambiguationData":[TD([[makeQuery(id+"F0.imprint","IMPRINT",EDGE,{"derivedFrom":subQ4}),-1.0]])]});}
            var Q3;
            Q3=makeQuery(id+"F0.imprint","IMPRINT",FACE,{"disambiguationData":[TD([[makeQuery(id+"F0.imprint","IMPRINT",EDGE,{"derivedFrom":sQuery(id+"F0.wireOp",EDGE,"E115.bottom")}),-1.0]])]});
            var Q4;
            Q4=makeQuery(id+"F0.imprint","IMPRINT",FACE,{"disambiguationData":[TD([[makeQuery(id+"F0.imprint","IMPRINT",EDGE,{"derivedFrom":sQuery(id+"F0.wireOp",EDGE,"E21.bottom")}),1.0]])]});
            var Q5;
            Q5=makeQuery(id+"F0.imprint","IMPRINT",FACE,{"disambiguationData":[TD([[makeQuery(id+"F0.imprint","IMPRINT",EDGE,{"derivedFrom":sQuery(id+"F0.wireOp",EDGE,"E50.MirrorCS")}),1.0]])]});
            var Q6;
            Q6=makeQuery(id+"F0.imprint","IMPRINT",FACE,{"disambiguationData":[TD([[makeQuery(id+"F0.imprint","IMPRINT",EDGE,{"derivedFrom":sQuery(id+"F0.wireOp",EDGE,"E45.MirrorCS")}),1.0]])]});
            var Q7;
            Q7=makeQuery(id+"F0.imprint","IMPRINT",FACE,{"disambiguationData":[TD([[makeQuery(id+"F0.imprint","IMPRINT",EDGE,{"derivedFrom":sQuery(id+"F0.wireOp",EDGE,"E67.MirrorCS")}),1.0]])]});
            var Q8;
            Q8=makeQuery(id+"F0.imprint","IMPRINT",FACE,{"disambiguationData":[TD([[makeQuery(id+"F0.imprint","IMPRINT",EDGE,{"derivedFrom":sQuery(id+"F0.wireOp",EDGE,"E83.MirrorCS")}),1.0]])]});
            var Q9;
            Q9=makeQuery(id+"F0.imprint","IMPRINT",FACE,{"disambiguationData":[TD([[makeQuery(id+"F0.imprint","IMPRINT",EDGE,{"derivedFrom":sQuery(id+"F0.wireOp",EDGE,"E0.0")}),-1.0]])]});
            extrude(context, id + "F1", {"entities" : qUnion([Q0, Q1, Q2, Q3, Q4, Q5, Q6, Q7, Q8, Q9]), "depth" : 4.45 * mm, "offsetDistance" : 25 * mm});
        }
    });
